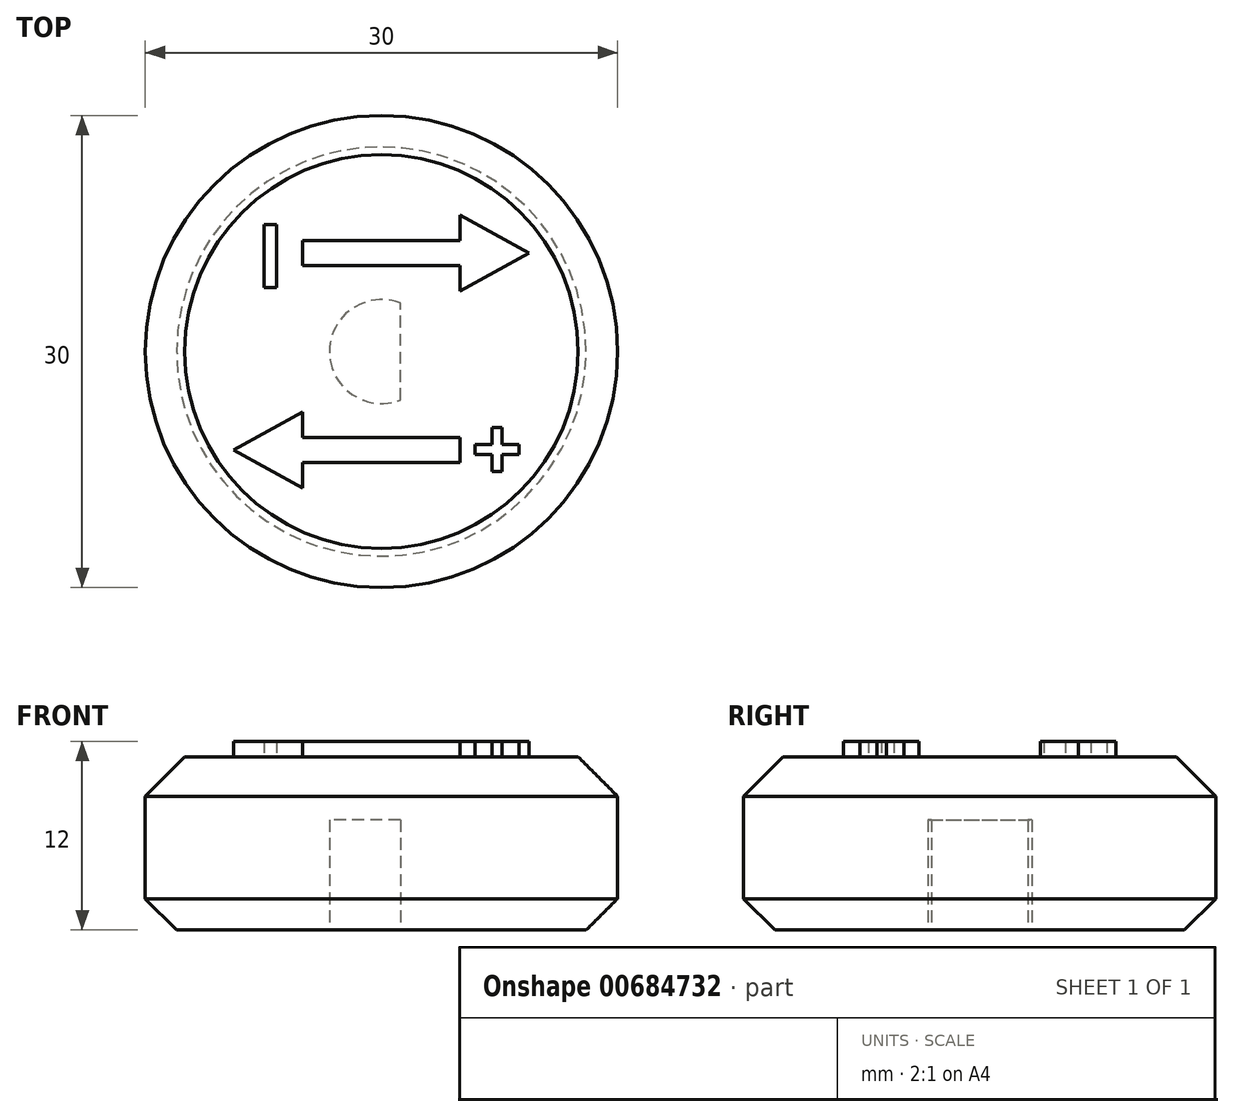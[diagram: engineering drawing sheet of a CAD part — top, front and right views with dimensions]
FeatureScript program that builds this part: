
annotation { "Feature Type Name" : "Feature", "Feature Type Description" : "" }
export const myFeature = defineFeature(function(context is Context, id is Id, definition is map)
    precondition{}
    {
        {
            var Q0;
            Q0=qCreatedBy(makeId("Top.planeOp"),FACE);
            var sketch = newSketch(context, id + "F0", { "sketchPlane" : qUnion([Q0])});
            skCircle(sketch, "E0", {"center": v(0, 0) * mm, "radius": 15 * mm});
            skSolve(sketch);
        }
        {
            var Q0;
            Q0 = qSketchRegion(id + "F0", true);
            extrude(context, id + "F1", {"entities" : qUnion([Q0]), "depth" : 11 * mm, "offsetDistance" : 25 * mm});
        }
        {
            var Q0;
            Q0=makeQuery(id+"F1.opExtrude","CAP_FACE",FACE,{"disambiguationData":[OSD([sQuery(id+"F0.wireOp",EDGE,"E0")])],"isStart":true});
            var sketch = newSketch(context, id + "F2", { "sketchPlane" : qUnion([Q0])});
            skArc(sketch, "E1", {"start": v(1.2, 3.07) * mm, "mid": v(-3.3, 0) * mm, "end": v(1.2, -3.07) * mm});
            skLineSegment(sketch, "E2", {"start": v(1.2, 3.07) * mm, "end": v(1.2, -3.07) * mm});
            skPoint(sketch, "E3", {"position": v(-3.3, 0) * mm});
            skSolve(sketch);
        }
        {
            var Q0;
            Q0 = qSketchRegion(id + "F2", true);
            extrude(context, id + "F3", {"entities" : qUnion([Q0]), "operationType" : NewBodyOperationType.REMOVE, "oppositeDirection" : true, "depth" : 7 * mm, "offsetDistance" : 25 * mm});
        }
        {
            var Q0;
            Q0=makeQuery(id+"F1.opExtrude","CAP_EDGE",EDGE,{"disambiguationData":[OSD([sQuery(id+"F0.wireOp",EDGE,"E0")])],"isStart":false});
            chamfer(context, id + "F4", {"entities" : qUnion([Q0]), "width" : 2.5 * mm, "tangentPropagation" : true});
        }
        {
            var Q0;
            Q0=makeQuery(id+"F1.opExtrude","CAP_EDGE",EDGE,{"disambiguationData":[OSD([sQuery(id+"F0.wireOp",EDGE,"E0")])],"isStart":true});
            chamfer(context, id + "F5", {"entities" : qUnion([Q0]), "width" : 2 * mm, "tangentPropagation" : true});
        }
        {
            var Q0;
            Q0=makeQuery(id+"F1.opExtrude","CAP_FACE",FACE,{"disambiguationData":[OSD([sQuery(id+"F0.wireOp",EDGE,"E0")])],"isStart":false});
            var sketch = newSketch(context, id + "F6", { "sketchPlane" : qUnion([Q0])});
            skLineSegment(sketch, "E4.bottom", {"start": v(-5, -5.45) * mm, "end": v(5, -5.45) * mm});
            skLineSegment(sketch, "E4.top", {"start": v(-5, -7.05) * mm, "end": v(5, -7.05) * mm});
            skLineSegment(sketch, "E4.left", {"start": v(-5, -5.45) * mm, "end": v(-5, -7.05) * mm});
            skLineSegment(sketch, "E4.right", {"start": v(5, -5.45) * mm, "end": v(5, -7.05) * mm});
            skLineSegment(sketch, "E5.bottom", {"start": v(5, 7.05) * mm, "end": v(-5, 7.05) * mm});
            skLineSegment(sketch, "E5.top", {"start": v(5, 5.45) * mm, "end": v(-5, 5.45) * mm});
            skLineSegment(sketch, "E5.left", {"start": v(5, 7.05) * mm, "end": v(5, 5.45) * mm});
            skLineSegment(sketch, "E5.right", {"start": v(-5, 7.05) * mm, "end": v(-5, 5.45) * mm});
            skPoint(sketch, "E6.endSnap0", {"position": v(-5, -6.25) * mm});
            skLineSegment(sketch, "E7", {"start": v(5, 5.45) * mm, "end": v(5, 3.85) * mm});
            skLineSegment(sketch, "E8", {"start": v(5, 3.85) * mm, "end": v(9.39, 6.25) * mm});
            skPoint(sketch, "E8.endSnap0", {"position": v(5, 6.25) * mm});
            skLineSegment(sketch, "E9", {"start": v(9.39, 6.25) * mm, "end": v(5, 8.65) * mm});
            skLineSegment(sketch, "E10", {"start": v(5, 8.65) * mm, "end": v(5, 7.05) * mm});
            skLineSegment(sketch, "E11", {"start": v(-5, -5.45) * mm, "end": v(-5, -3.85) * mm});
            skLineSegment(sketch, "E12", {"start": v(-5, -3.85) * mm, "end": v(-9.39, -6.25) * mm});
            skLineSegment(sketch, "E13", {"start": v(-9.39, -6.25) * mm, "end": v(-5, -8.65) * mm});
            skLineSegment(sketch, "E14", {"start": v(-5, -8.65) * mm, "end": v(-5, -7.05) * mm});
            skText(sketch, "E15", { "text": "+", "fontName": "OpenSans-Bold.ttf"});
            skLineSegment(sketch, "E16.bottom", {"start": v(-6.66, 8.07) * mm, "end": v(-7.46, 8.07) * mm});
            skLineSegment(sketch, "E16.top", {"start": v(-6.66, 4.07) * mm, "end": v(-7.46, 4.07) * mm});
            skLineSegment(sketch, "E16.left", {"start": v(-6.66, 8.07) * mm, "end": v(-6.66, 4.07) * mm});
            skLineSegment(sketch, "E16.right", {"start": v(-7.46, 8.07) * mm, "end": v(-7.46, 4.07) * mm});
            const initialGuessF6  = {"E15": [0.0057, -0.00825, 1, 0, 0.00415]};
            skSetInitialGuess(sketch, initialGuessF6);
            skSolve(sketch);
        }
        {
            var Q0;
            Q0 = qSketchRegion(id + "F6", true);
            extrude(context, id + "F7", {"entities" : qUnion([Q0]), "operationType" : NewBodyOperationType.ADD, "depth" : 1 * mm, "offsetDistance" : 25 * mm});
        }
    });
